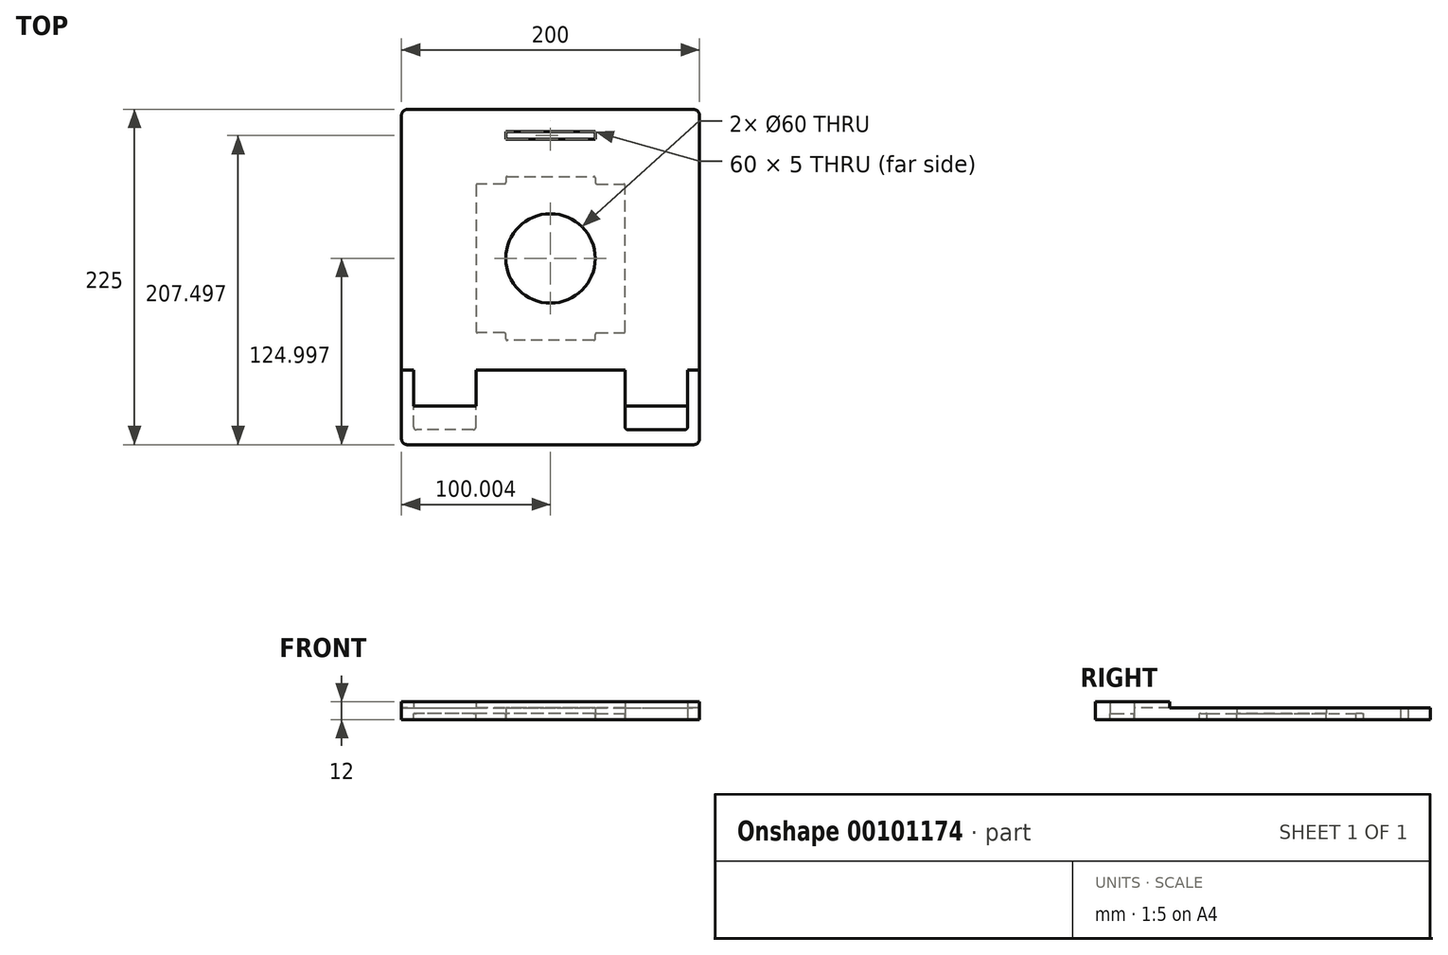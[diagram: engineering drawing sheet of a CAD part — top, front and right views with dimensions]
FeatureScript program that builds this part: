
annotation { "Feature Type Name" : "Feature", "Feature Type Description" : "" }
export const myFeature = defineFeature(function(context is Context, id is Id, definition is map)
    precondition{}
    {
        {
            assignVariable(context, id + "F0", {"name" : "thickness", "anyValue" : 4});
        }
        {
            var Q0;
            Q0=qCreatedBy(makeId("Top.planeOp"),FACE);
            var sketch = newSketch(context, id + "F1", { "sketchPlane" : qUnion([Q0])});
            skLineSegment(sketch, "E0.bottom", {"start": v(57.94, -40.82) * mm, "end": v(249.94, -40.82) * mm});
            skLineSegment(sketch, "E0.top", {"start": v(57.94, -265.82) * mm, "end": v(249.94, -265.82) * mm});
            skLineSegment(sketch, "E0.left", {"start": v(53.94, -44.82) * mm, "end": v(53.94, -261.82) * mm});
            skLineSegment(sketch, "E0.right", {"start": v(253.94, -44.82) * mm, "end": v(253.94, -261.82) * mm});
            skLineSegment(sketch, "E1", {"start": v(153.94, -40.82) * mm, "end": v(153.94, -265.82) * mm, "construction": true});
            skLineSegment(sketch, "E2", {"start": v(53.94, -140.82) * mm, "end": v(253.94, -140.82) * mm, "construction": true});
            skCircle(sketch, "E3", {"center": v(153.94, -140.82) * mm, "radius": 30 * mm});
            skPoint(sketch, "E4", {"position": v(123.94, -55.82) * mm});
            skPoint(sketch, "E5", {"position": v(123.94, -60.82) * mm});
            skPoint(sketch, "E6", {"position": v(153.94, -60.82) * mm});
            skPoint(sketch, "E7", {"position": v(153.94, -55.82) * mm});
            skLineSegment(sketch, "E8.bottom", {"start": v(123.94, -55.82) * mm, "end": v(153.94, -55.82) * mm});
            skLineSegment(sketch, "E8.top", {"start": v(123.94, -60.82) * mm, "end": v(153.94, -60.82) * mm});
            skLineSegment(sketch, "E8.left", {"start": v(123.94, -55.82) * mm, "end": v(123.94, -60.82) * mm});
            skLineSegment(sketch, "E9.bottom", {"start": v(101.94, -255.82) * mm, "end": v(63.94, -255.82) * mm});
            skLineSegment(sketch, "E9.top", {"start": v(103.94, -239.82) * mm, "end": v(61.94, -239.82) * mm});
            skLineSegment(sketch, "E9.left", {"start": v(103.94, -253.82) * mm, "end": v(103.94, -239.82) * mm});
            skLineSegment(sketch, "E9.right", {"start": v(61.94, -253.82) * mm, "end": v(61.94, -239.82) * mm});
            skLineSegment(sketch, "E10", {"start": v(153.94, -85.82) * mm, "end": v(124.94, -85.82) * mm});
            skLineSegment(sketch, "E11", {"start": v(123.94, -86.82) * mm, "end": v(123.94, -89.82) * mm});
            skLineSegment(sketch, "E12", {"start": v(122.94, -90.82) * mm, "end": v(104.94, -90.82) * mm});
            skLineSegment(sketch, "E13", {"start": v(103.94, -91.82) * mm, "end": v(103.94, -140.82) * mm});
            skPoint(sketch, "E14.visualSharp", {"position": v(53.94, -40.82) * mm});
            skArc(sketch, "E14.filletArc", {"start": v(57.94, -40.82) * mm, "mid": v(55.12, -42) * mm, "end": v(53.94, -44.82) * mm});
            skPoint(sketch, "E15.visualSharp", {"position": v(253.94, -40.82) * mm});
            skArc(sketch, "E15.filletArc", {"start": v(253.94, -44.82) * mm, "mid": v(252.77, -42) * mm, "end": v(249.94, -40.82) * mm});
            skPoint(sketch, "E16.visualSharp", {"position": v(253.94, -265.82) * mm});
            skArc(sketch, "E16.filletArc", {"start": v(249.94, -265.82) * mm, "mid": v(252.77, -264.65) * mm, "end": v(253.94, -261.82) * mm});
            skPoint(sketch, "E17.visualSharp", {"position": v(53.94, -265.82) * mm});
            skArc(sketch, "E17.filletArc", {"start": v(53.94, -261.82) * mm, "mid": v(55.12, -264.65) * mm, "end": v(57.94, -265.82) * mm});
            skPoint(sketch, "E18.visualSharp", {"position": v(61.94, -255.82) * mm});
            skArc(sketch, "E18.filletArc", {"start": v(61.94, -253.82) * mm, "mid": v(62.53, -255.24) * mm, "end": v(63.94, -255.82) * mm});
            skPoint(sketch, "E19.visualSharp", {"position": v(103.94, -255.82) * mm});
            skArc(sketch, "E19.filletArc", {"start": v(101.94, -255.82) * mm, "mid": v(103.36, -255.24) * mm, "end": v(103.94, -253.82) * mm});
            skPoint(sketch, "E20.visualSharp", {"position": v(123.94, -85.82) * mm});
            skArc(sketch, "E20.filletArc", {"start": v(124.94, -85.82) * mm, "mid": v(124.24, -86.12) * mm, "end": v(123.94, -86.82) * mm});
            skPoint(sketch, "E21.visualSharp", {"position": v(123.94, -90.82) * mm});
            skArc(sketch, "E21.filletArc", {"start": v(122.94, -90.82) * mm, "mid": v(123.65, -90.53) * mm, "end": v(123.94, -89.82) * mm});
            skPoint(sketch, "E22.visualSharp", {"position": v(103.94, -90.82) * mm});
            skArc(sketch, "E22.filletArc", {"start": v(104.94, -90.82) * mm, "mid": v(104.24, -91.12) * mm, "end": v(103.94, -91.82) * mm});
            skArc(sketch, "E23.MirrorCS", {"start": v(104.94, -190.82) * mm, "mid": v(104.24, -190.53) * mm, "end": v(103.94, -189.82) * mm});
            skArc(sketch, "E24.MirrorCS", {"start": v(122.94, -190.82) * mm, "mid": v(123.65, -191.12) * mm, "end": v(123.94, -191.82) * mm});
            skArc(sketch, "E25.MirrorCS", {"start": v(124.94, -195.82) * mm, "mid": v(124.24, -195.53) * mm, "end": v(123.94, -194.82) * mm});
            skLineSegment(sketch, "E26.MirrorCS", {"start": v(123.94, -194.82) * mm, "end": v(123.94, -191.82) * mm});
            skLineSegment(sketch, "E27.MirrorCS", {"start": v(153.94, -195.82) * mm, "end": v(124.94, -195.82) * mm});
            skLineSegment(sketch, "E28.MirrorCS", {"start": v(103.94, -189.82) * mm, "end": v(103.94, -140.82) * mm});
            skLineSegment(sketch, "E29.MirrorCS", {"start": v(122.94, -190.82) * mm, "end": v(104.94, -190.82) * mm});
            skPoint(sketch, "E30.MirrorP", {"position": v(123.94, -195.82) * mm});
            skPoint(sketch, "E31.MirrorP", {"position": v(123.94, -190.82) * mm});
            skPoint(sketch, "E32.MirrorP", {"position": v(103.94, -190.82) * mm});
            skArc(sketch, "E33.MirrorCS", {"start": v(184.94, -190.82) * mm, "mid": v(184.24, -191.12) * mm, "end": v(183.94, -191.82) * mm});
            skArc(sketch, "E34.MirrorCS", {"start": v(184.94, -90.82) * mm, "mid": v(184.24, -90.53) * mm, "end": v(183.94, -89.82) * mm});
            skLineSegment(sketch, "E35.MirrorCS", {"start": v(183.94, -194.82) * mm, "end": v(183.94, -191.82) * mm});
            skArc(sketch, "E36.MirrorCS", {"start": v(182.94, -195.82) * mm, "mid": v(183.65, -195.53) * mm, "end": v(183.94, -194.82) * mm});
            skLineSegment(sketch, "E37.MirrorCS", {"start": v(183.94, -86.82) * mm, "end": v(183.94, -89.82) * mm});
            skArc(sketch, "E38.MirrorCS", {"start": v(182.94, -85.82) * mm, "mid": v(183.65, -86.12) * mm, "end": v(183.94, -86.82) * mm});
            skArc(sketch, "E39.MirrorCS", {"start": v(202.94, -90.82) * mm, "mid": v(203.65, -91.12) * mm, "end": v(203.94, -91.82) * mm});
            skArc(sketch, "E40.MirrorCS", {"start": v(202.94, -190.82) * mm, "mid": v(203.65, -190.53) * mm, "end": v(203.94, -189.82) * mm});
            skPoint(sketch, "E41.MirrorP", {"position": v(183.94, -190.82) * mm});
            skLineSegment(sketch, "E42.MirrorCS", {"start": v(203.94, -189.82) * mm, "end": v(203.94, -140.82) * mm});
            skLineSegment(sketch, "E43.MirrorCS", {"start": v(184.94, -90.82) * mm, "end": v(202.94, -90.82) * mm});
            skPoint(sketch, "E44.MirrorP", {"position": v(183.94, -85.82) * mm});
            skPoint(sketch, "E45.MirrorP", {"position": v(203.94, -90.82) * mm});
            skLineSegment(sketch, "E46.MirrorCS", {"start": v(184.94, -190.82) * mm, "end": v(202.94, -190.82) * mm});
            skLineSegment(sketch, "E47.MirrorCS", {"start": v(203.94, -91.82) * mm, "end": v(203.94, -140.82) * mm});
            skLineSegment(sketch, "E48.MirrorCS", {"start": v(153.94, -195.82) * mm, "end": v(182.94, -195.82) * mm});
            skLineSegment(sketch, "E49.MirrorCS", {"start": v(153.94, -85.82) * mm, "end": v(182.94, -85.82) * mm});
            skPoint(sketch, "E50.MirrorP", {"position": v(203.94, -190.82) * mm});
            skPoint(sketch, "E51.MirrorP", {"position": v(183.94, -90.82) * mm});
            skPoint(sketch, "E52.MirrorP", {"position": v(183.94, -195.82) * mm});
            skArc(sketch, "E53.MirrorCS", {"start": v(205.94, -255.82) * mm, "mid": v(204.53, -255.24) * mm, "end": v(203.94, -253.82) * mm});
            skArc(sketch, "E54.MirrorCS", {"start": v(245.94, -253.82) * mm, "mid": v(245.36, -255.24) * mm, "end": v(243.94, -255.82) * mm});
            skPoint(sketch, "E55.MirrorP", {"position": v(203.94, -255.82) * mm});
            skLineSegment(sketch, "E56.MirrorCS", {"start": v(203.94, -253.82) * mm, "end": v(203.94, -239.82) * mm});
            skLineSegment(sketch, "E57.MirrorCS", {"start": v(203.94, -239.82) * mm, "end": v(245.94, -239.82) * mm});
            skLineSegment(sketch, "E58.MirrorCS", {"start": v(245.94, -253.82) * mm, "end": v(245.94, -239.82) * mm});
            skLineSegment(sketch, "E59.MirrorCS", {"start": v(205.94, -255.82) * mm, "end": v(243.94, -255.82) * mm});
            skPoint(sketch, "E60.MirrorP", {"position": v(245.94, -255.82) * mm});
            skPoint(sketch, "E61.MirrorP", {"position": v(183.94, -60.82) * mm});
            skLineSegment(sketch, "E62.MirrorCS", {"start": v(183.94, -55.82) * mm, "end": v(183.94, -60.82) * mm});
            skLineSegment(sketch, "E63.MirrorCS", {"start": v(183.94, -55.82) * mm, "end": v(153.94, -55.82) * mm});
            skLineSegment(sketch, "E64.MirrorCS", {"start": v(183.94, -60.82) * mm, "end": v(153.94, -60.82) * mm});
            skPoint(sketch, "E65.MirrorP", {"position": v(183.94, -55.82) * mm});
            skLineSegment(sketch, "E66.top", {"start": v(61.94, -239.82) * mm, "end": v(103.94, -239.82) * mm});
            skLineSegment(sketch, "E66.left", {"start": v(61.94, -215.82) * mm, "end": v(61.94, -239.82) * mm});
            skLineSegment(sketch, "E66.right", {"start": v(103.94, -215.82) * mm, "end": v(103.94, -239.82) * mm});
            skLineSegment(sketch, "E67.MirrorCS", {"start": v(203.94, -215.82) * mm, "end": v(203.94, -239.82) * mm});
            skLineSegment(sketch, "E68.MirrorCS", {"start": v(245.94, -215.82) * mm, "end": v(245.94, -239.82) * mm});
            skLineSegment(sketch, "E69", {"start": v(61.94, -215.82) * mm, "end": v(53.94, -215.82) * mm});
            skLineSegment(sketch, "E70", {"start": v(103.94, -215.82) * mm, "end": v(203.94, -215.82) * mm});
            skLineSegment(sketch, "E71", {"start": v(245.94, -215.82) * mm, "end": v(253.94, -215.82) * mm});
            skLineSegment(sketch, "E72.bottom", {"start": v(63.94, -255.82) * mm, "end": v(101.94, -255.82) * mm});
            skSolve(sketch);
        }
        {
            var Q0;
            Q0=makeQuery(id+"F1.imprint","IMPRINT",FACE,{"disambiguationData":[TD([[makeQuery(id+"F1.imprint","IMPRINT",EDGE,{"derivedFrom":sQuery(id+"F1.wireOp",EDGE,"E0.bottom")}),-1.0]])]});
            var Q1;
            Q1=makeQuery(id+"F1.imprint","IMPRINT",FACE,{"disambiguationData":[TD([[makeQuery(id+"F1.imprint","IMPRINT",EDGE,{"derivedFrom":sQuery(id+"F1.wireOp",EDGE,"E57.MirrorCS")}),1.0]])]});
            var Q2;
            Q2=makeQuery(id+"F1.imprint","IMPRINT",FACE,{"disambiguationData":[TD([[makeQuery(id+"F1.imprint","IMPRINT",EDGE,{"derivedFrom":sQuery(id+"F1.wireOp",EDGE,"E66.top")}),1.0]])]});
            var Q3;
            Q3=makeQuery(id+"F1.imprint","IMPRINT",FACE,{"disambiguationData":[TD([[makeQuery(id+"F1.imprint","IMPRINT",EDGE,{"derivedFrom":sQuery(id+"F1.wireOp",EDGE,"E9.bottom")}),-1.0]])]});
            var Q4;
            Q4=makeQuery(id+"F1.imprint","IMPRINT",FACE,{"disambiguationData":[TD([[makeQuery(id+"F1.imprint","IMPRINT",EDGE,{"derivedFrom":sQuery(id+"F1.wireOp",EDGE,"E53.MirrorCS")}),-1.0]])]});
            var Q5;
            Q5=makeQuery(id+"F1.imprint","IMPRINT",FACE,{"disambiguationData":[TD([[makeQuery(id+"F1.imprint","IMPRINT",EDGE,{"derivedFrom":sQuery(id+"F1.wireOp",EDGE,"E3")}),-1.0]])]});
            extrude(context, id + "F2", {"entities" : qUnion([Q0, Q1, Q2, Q3, Q4, Q5]), "depth" : (getVariable(context, 'thickness')) * mm});
        }
        {
            var Q0;
            Q0=makeQuery(id+"F1.imprint","IMPRINT",FACE,{"disambiguationData":[TD([[makeQuery(id+"F1.imprint","IMPRINT",EDGE,{"derivedFrom":sQuery(id+"F1.wireOp",EDGE,"E3")}),-1.0]])]});
            extrude(context, id + "F3", {"entities" : qUnion([Q0]), "oppositeDirection" : true, "depth" : (getVariable(context, 'thickness')) * mm});
        }
        {
            var Q0;
            Q0=makeQuery(id+"F1.imprint","IMPRINT",FACE,{"disambiguationData":[TD([[makeQuery(id+"F1.imprint","IMPRINT",EDGE,{"derivedFrom":sQuery(id+"F1.wireOp",EDGE,"E0.top")}),1.0]])]});
            var Q1;
            Q1=makeQuery(id+"F1.imprint","IMPRINT",FACE,{"disambiguationData":[TD([[makeQuery(id+"F1.imprint","IMPRINT",EDGE,{"derivedFrom":sQuery(id+"F1.wireOp",EDGE,"E0.bottom")}),-1.0]])]});
            var Q2;
            Q2=makeQuery(id+"F1.imprint","IMPRINT",FACE,{"disambiguationData":[TD([[makeQuery(id+"F1.imprint","IMPRINT",EDGE,{"derivedFrom":sQuery(id+"F1.wireOp",EDGE,"E66.top")}),1.0]])]});
            var Q3;
            Q3=makeQuery(id+"F1.imprint","IMPRINT",FACE,{"disambiguationData":[TD([[makeQuery(id+"F1.imprint","IMPRINT",EDGE,{"derivedFrom":sQuery(id+"F1.wireOp",EDGE,"E57.MirrorCS")}),1.0]])]});
            extrude(context, id + "F4", {"entities" : qUnion([Q0, Q1, Q2, Q3]), "oppositeDirection" : true, "depth" : (getVariable(context, 'thickness')) * mm});
        }
        {
            var Q0;
            Q0=makeQuery(id+"F1.imprint","IMPRINT",FACE,{"disambiguationData":[TD([[makeQuery(id+"F1.imprint","IMPRINT",EDGE,{"derivedFrom":sQuery(id+"F1.wireOp",EDGE,"E9.bottom")}),-1.0]])]});
            var Q1;
            Q1=makeQuery(id+"F1.imprint","IMPRINT",FACE,{"disambiguationData":[TD([[makeQuery(id+"F1.imprint","IMPRINT",EDGE,{"derivedFrom":sQuery(id+"F1.wireOp",EDGE,"E53.MirrorCS")}),-1.0]])]});
            extrude(context, id + "F5", {"entities" : qUnion([Q0, Q1]), "operationType" : NewBodyOperationType.ADD, "depth" : (2 * getVariable(context, 'thickness')) * mm});
        }
    });
